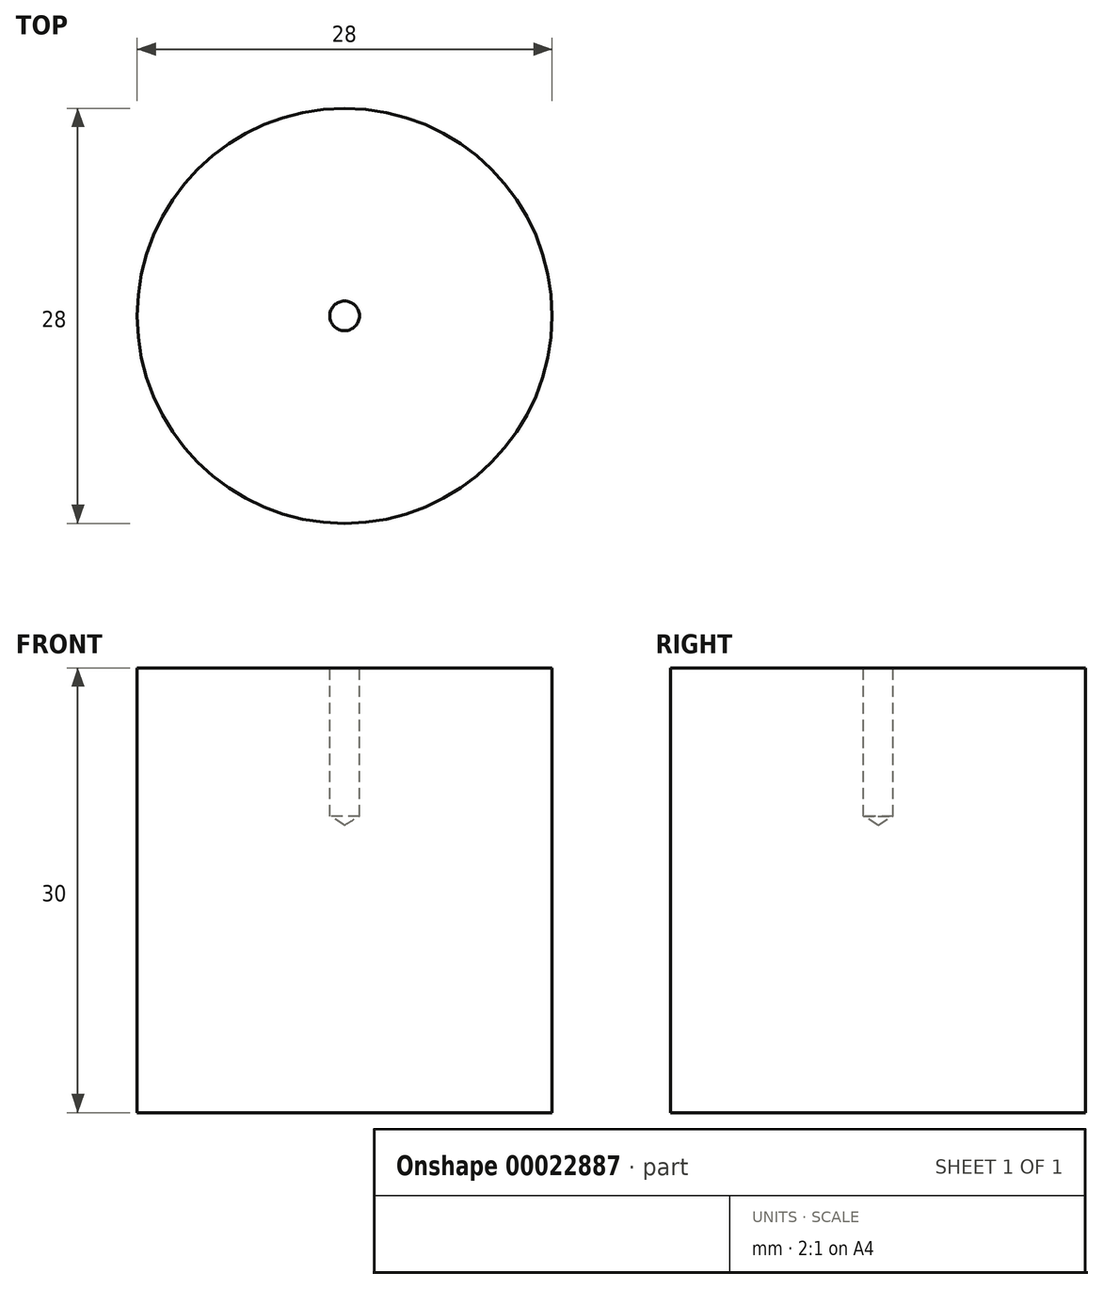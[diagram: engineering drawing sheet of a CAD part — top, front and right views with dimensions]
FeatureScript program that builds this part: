
annotation { "Feature Type Name" : "Feature", "Feature Type Description" : "" }
export const myFeature = defineFeature(function(context is Context, id is Id, definition is map)
    precondition{}
    {
        {
            var Q0;
            Q0=qCreatedBy(makeId("Top.planeOp"),FACE);
            var sketch = newSketch(context, id + "F0", { "sketchPlane" : qUnion([Q0])});
            skCircle(sketch, "E0", {"center": v(0, 0) * mm, "radius": 14 * mm});
            skSolve(sketch);
        }
        {
            var Q0;
            Q0=makeQuery(id+"F0.imprint","IMPRINT",FACE,{"disambiguationData":[TD([[makeQuery(id+"F0.imprint","IMPRINT",EDGE,{"derivedFrom":sQuery(id+"F0.wireOp",EDGE,"E0")}),1.0]])]});
            extrude(context, id + "F1", {"entities" : qUnion([Q0]), "depth" : 30 * mm});
        }
        {
            var Q0;
            Q0=makeQuery(id+"F1.opExtrude","CAP_FACE",FACE,{"disambiguationData":[OSD([sQuery(id+"F0.wireOp",EDGE,"E0")])],"isStart":false});
            var sketch = newSketch(context, id + "F2", { "sketchPlane" : qUnion([Q0])});
            skPoint(sketch, "E1", {"position": v(0, 0) * mm});
            skSolve(sketch);
        }
        {
            var Q0;
            Q0=sQuery(id+"F2.wireOp",VERTEX,"E1");
            var Q1;
            Q1=makeQuery(id+"F1.opExtrude","SWEPT_BODY",BODY,{"disambiguationData":[OSD([sQuery(id+"F0.wireOp",EDGE,"E0")])]});
            hole(context, id + "F3", {"style" : HoleStyle.SIMPLE, "holeDiameter" : 2 * mm, "endStyle" : HoleEndStyle.BLIND, "holeDepth" : 10 * mm, "locations" : qUnion([Q0]), "scope" : qUnion([Q1])});
        }
    });
